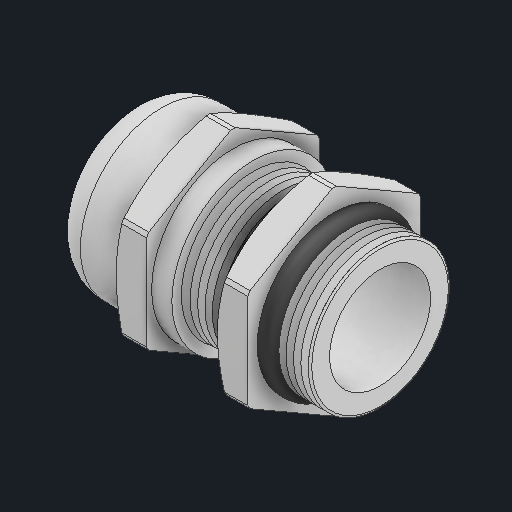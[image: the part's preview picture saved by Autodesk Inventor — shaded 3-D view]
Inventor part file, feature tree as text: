
AUTODESK INVENTOR PART (.ipt)
format: ipt  version: 2025 (Build 290162000, 162)  size: 283,136 bytes
history: native  units: in
note: dims shown in document units (in); Inventor stores cm internally (conversion verified against a paired STEP export)
features: other x1, revolve x1
ambient origin geometry x8: Origin, YZ Plane, XZ Plane, XY Plane, X Axis, Y Axis, Z Axis, Center Point
bodies: Solid1 (feature_tree), Solid2 (feature_tree)
feature tree (2):
  other  "REDUCED THREAD CUT"
  revolve  "Revolve3"  [1 undecoded]
note: 1 required parameter value undecoded (feature->parameter linkage not recoverable at this tier; creation-order binding heuristic only, values carry confidence <= 0.55)
